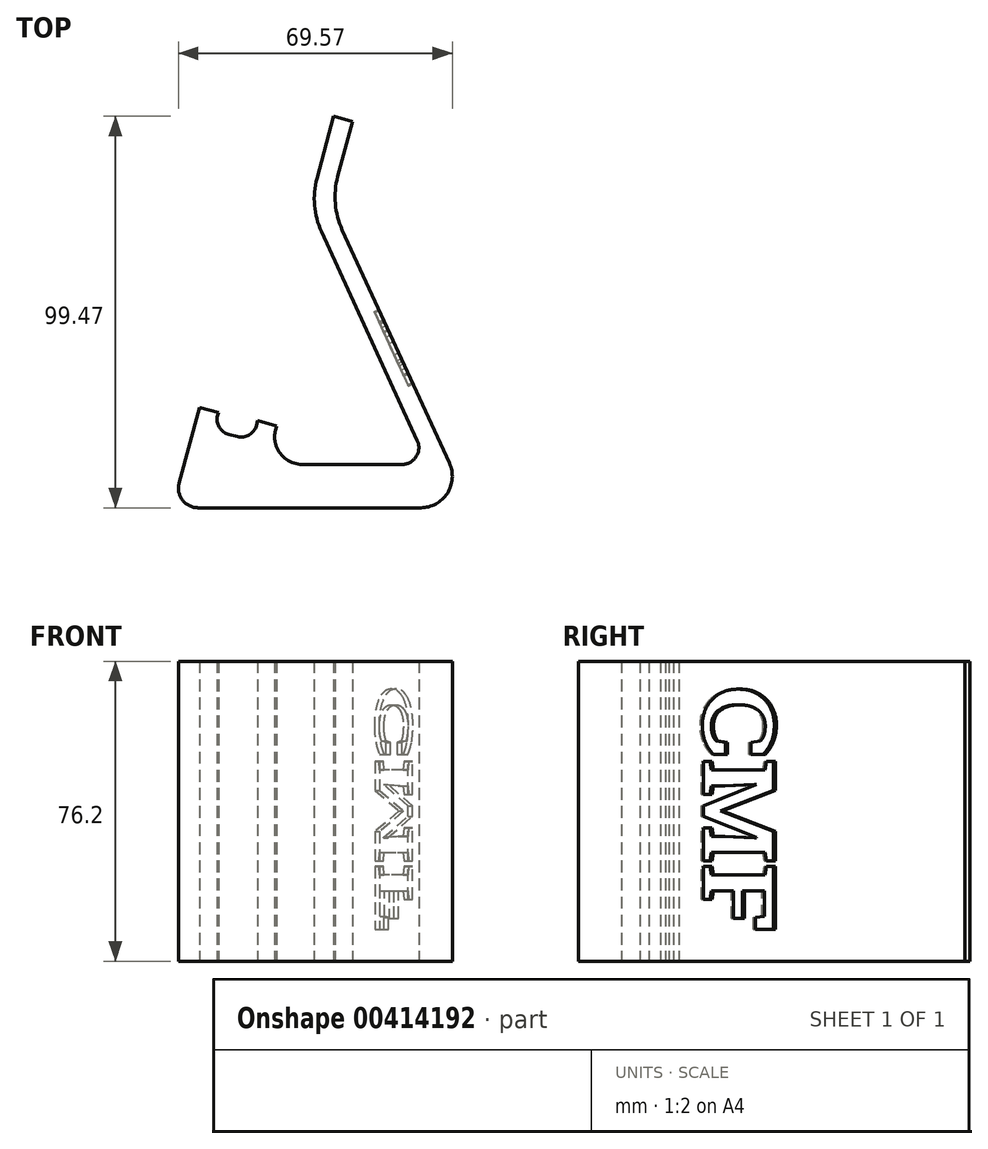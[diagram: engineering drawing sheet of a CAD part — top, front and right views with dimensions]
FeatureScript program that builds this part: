
annotation { "Feature Type Name" : "Feature", "Feature Type Description" : "" }
export const myFeature = defineFeature(function(context is Context, id is Id, definition is map)
    precondition{}
    {
        {
            var Q0;
            Q0=qCreatedBy(makeId("Top.planeOp"),FACE);
            var sketch = newSketch(context, id + "F0", { "sketchPlane" : qUnion([Q0])});
            skPoint(sketch, "E0.0", {"position": v(34, 9.46) * mm});
            skPoint(sketch, "E1.0", {"position": v(34, 4.63) * mm});
            skPoint(sketch, "E2.0", {"position": v(41, 0.4) * mm});
            skPoint(sketch, "E3.0", {"position": v(41, 5.7) * mm});
            skPoint(sketch, "E4.0", {"position": v(41, 1.55) * mm});
            skPoint(sketch, "E5.0", {"position": v(41, 6.84) * mm});
            skPoint(sketch, "E6.0", {"position": v(41, 25.9) * mm});
            skPoint(sketch, "E7.0", {"position": v(41, 34.06) * mm});
            skPoint(sketch, "E8.0", {"position": v(41, 26.8) * mm});
            skPoint(sketch, "E9.0", {"position": v(41, -29.78) * mm});
            skPoint(sketch, "E10.0", {"position": v(41, -34.61) * mm});
            skPoint(sketch, "E11.0", {"position": v(36, -29.46) * mm});
            skPoint(sketch, "E12.0", {"position": v(36, -24.63) * mm});
            skPoint(sketch, "E13.0", {"position": v(39.31, -24.92) * mm});
            skPoint(sketch, "E14.0", {"position": v(41, -21.93) * mm});
            skPoint(sketch, "E15.0", {"position": v(41, -19.79) * mm});
            skPoint(sketch, "E16.0", {"position": v(36, -14.63) * mm});
            skPoint(sketch, "E17.0", {"position": v(36, -9.8) * mm});
            skPoint(sketch, "E18.0", {"position": v(41, -9.91) * mm});
            skPoint(sketch, "E19.0", {"position": v(41, -3.31) * mm});
            skPoint(sketch, "E20.0", {"position": v(41, 21.97) * mm});
            skLineSegment(sketch, "E21", {"start": v(-24.63, -53.35) * mm, "end": v(-24.92, -54.57) * mm});
            skLineSegment(sketch, "E22", {"start": v(-14.63, -55.46) * mm, "end": v(-9.8, -56.75) * mm});
            skLineSegment(sketch, "E23", {"start": v(-21.93, -58.96) * mm, "end": v(-19.79, -59.5) * mm});
            skLineSegment(sketch, "E24", {"start": v(-29.46, -52.05) * mm, "end": v(-24.63, -53.35) * mm});
            skLineSegment(sketch, "E25", {"start": v(-29.46, -52.05) * mm, "end": v(-34.61, -71.28) * mm});
            skLineSegment(sketch, "E26", {"start": v(-29.78, -77.58) * mm, "end": v(26.8, -77.58) * mm});
            skLineSegment(sketch, "E27", {"start": v(-3.31, -66.58) * mm, "end": v(21.97, -66.58) * mm});
            skLineSegment(sketch, "E28", {"start": v(25.9, -60.45) * mm, "end": v(1.55, -7.41) * mm});
            skLineSegment(sketch, "E29", {"start": v(6.84, -6.96) * mm, "end": v(34.06, -66.24) * mm});
            skLineSegment(sketch, "E30", {"start": v(9.46, 20.6) * mm, "end": v(4.63, 21.9) * mm});
            skLineSegment(sketch, "E31", {"start": v(4.63, 21.9) * mm, "end": v(0.4, 6.11) * mm});
            skLineSegment(sketch, "E32", {"start": v(5.7, 6.56) * mm, "end": v(9.46, 20.6) * mm});
            skArc(sketch, "E33", {"start": v(-19.79, -59.5) * mm, "mid": v(-16.8, -59.06) * mm, "end": v(-14.96, -56.66) * mm});
            skLineSegment(sketch, "E34", {"start": v(-14.96, -56.66) * mm, "end": v(-14.63, -55.46) * mm});
            skArc(sketch, "E35", {"start": v(-24.92, -54.57) * mm, "mid": v(-24.26, -57.33) * mm, "end": v(-21.93, -58.96) * mm});
            skLineSegment(sketch, "E36", {"start": v(-9.8, -56.75) * mm, "end": v(-10.12, -57.96) * mm});
            skArc(sketch, "E37", {"start": v(-10.12, -57.96) * mm, "mid": v(-10.33, -59.95) * mm, "end": v(-9.91, -61.9) * mm});
            skArc(sketch, "E38", {"start": v(-9.91, -61.9) * mm, "mid": v(-7.36, -65.29) * mm, "end": v(-3.31, -66.58) * mm});
            skArc(sketch, "E39", {"start": v(-34.61, -71.28) * mm, "mid": v(-33.75, -75.62) * mm, "end": v(-29.78, -77.58) * mm});
            skArc(sketch, "E40", {"start": v(26.8, -77.58) * mm, "mid": v(33.53, -73.9) * mm, "end": v(34.06, -66.24) * mm});
            skArc(sketch, "E41", {"start": v(5.7, 6.56) * mm, "mid": v(5.09, -0.3) * mm, "end": v(6.84, -6.96) * mm});
            skArc(sketch, "E42", {"start": v(0.4, 6.11) * mm, "mid": v(-0.2, -0.75) * mm, "end": v(1.55, -7.41) * mm});
            skArc(sketch, "E43", {"start": v(21.97, -66.58) * mm, "mid": v(25.61, -64.59) * mm, "end": v(25.9, -60.45) * mm});
            skSolve(sketch);
        }
        {
            var Q0;
            Q0=makeQuery(id+"F0.imprint","IMPRINT",FACE,{"disambiguationData":[TD([[makeQuery(id+"F0.imprint","IMPRINT",EDGE,{"derivedFrom":sQuery(id+"F0.wireOp",EDGE,"E21")}),-1.0]])]});
            extrude(context, id + "F1", {"entities" : qUnion([Q0]), "endBound" : BoundingType.SYMMETRIC, "depth" : 76.2 * mm});
        }
        {
            var Q0;
            Q0=makeQuery(id+"F1.opExtrude","SWEPT_FACE",FACE,{"disambiguationData":[OSD([sQuery(id+"F0.wireOp",EDGE,"E29")])]});
            var sketch = newSketch(context, id + "F2", { "sketchPlane" : qUnion([Q0])});
            skText(sketch, "E44", { "text": "CMF", "fontName": "RobotoSlab-Bold.ttf"});
            const initialGuessF2  = {"E44": [-0.0519, 0.03175, 0, -1, 0.02037]};
            skSetInitialGuess(sketch, initialGuessF2);
            skSolve(sketch);
        }
        {
            var Q0;
            Q0 = qSketchRegion(id + "F2", true);
            extrude(context, id + "F3", {"entities" : qUnion([Q0]), "operationType" : NewBodyOperationType.REMOVE, "oppositeDirection" : true, "depth" : 1.27 * mm});
        }
    });
